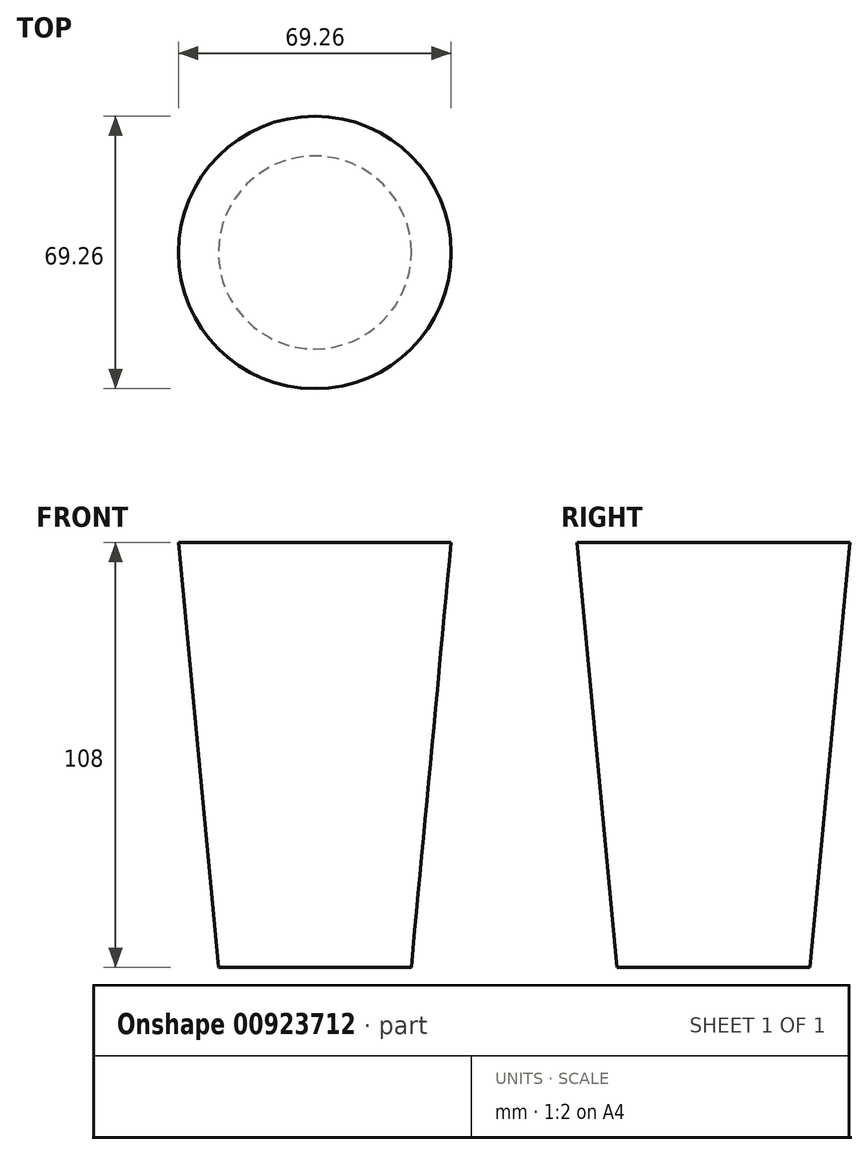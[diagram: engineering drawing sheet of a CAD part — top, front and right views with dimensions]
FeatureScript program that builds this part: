
annotation { "Feature Type Name" : "Feature", "Feature Type Description" : "" }
export const myFeature = defineFeature(function(context is Context, id is Id, definition is map)
    precondition{}
    {
        {
            var Q0;
            Q0=qCreatedBy(makeId("Top.planeOp"),FACE);
            var sketch = newSketch(context, id + "F0", { "sketchPlane" : qUnion([Q0])});
            skCircle(sketch, "E0", {"center": v(0, 0) * mm, "radius": 24.5 * mm});
            skSolve(sketch);
        }
        {
            var Q0;
            Q0=qCreatedBy(makeId("Top.planeOp"),FACE);
            cPlane(context, id + "F1", {"entities" : qUnion([Q0]), "cplaneType" : CPlaneType.OFFSET, "offset" : 108 * mm, "width" : 150 * mm, "height" : 150 * mm});
        }
        {
            var Q0;
            Q0=qCreatedBy(id+"F1.planeOp",FACE);
            var sketch = newSketch(context, id + "F2", { "sketchPlane" : qUnion([Q0])});
            skCircle(sketch, "E1", {"center": v(0, 0) * mm, "radius": 34.63 * mm});
            skSolve(sketch);
        }
        {
            var Q0;
            Q0 = qSketchRegion(id + "F0", true);
            var Q1;
            Q1 = qSketchRegion(id + "F2", true);
            loft(context, id + "F3", {"sheetProfilesArray" : [{ "sheetProfileEntities" : qUnion([Q0]) }, { "sheetProfileEntities" : qUnion([Q1]) }]});
        }
    });
